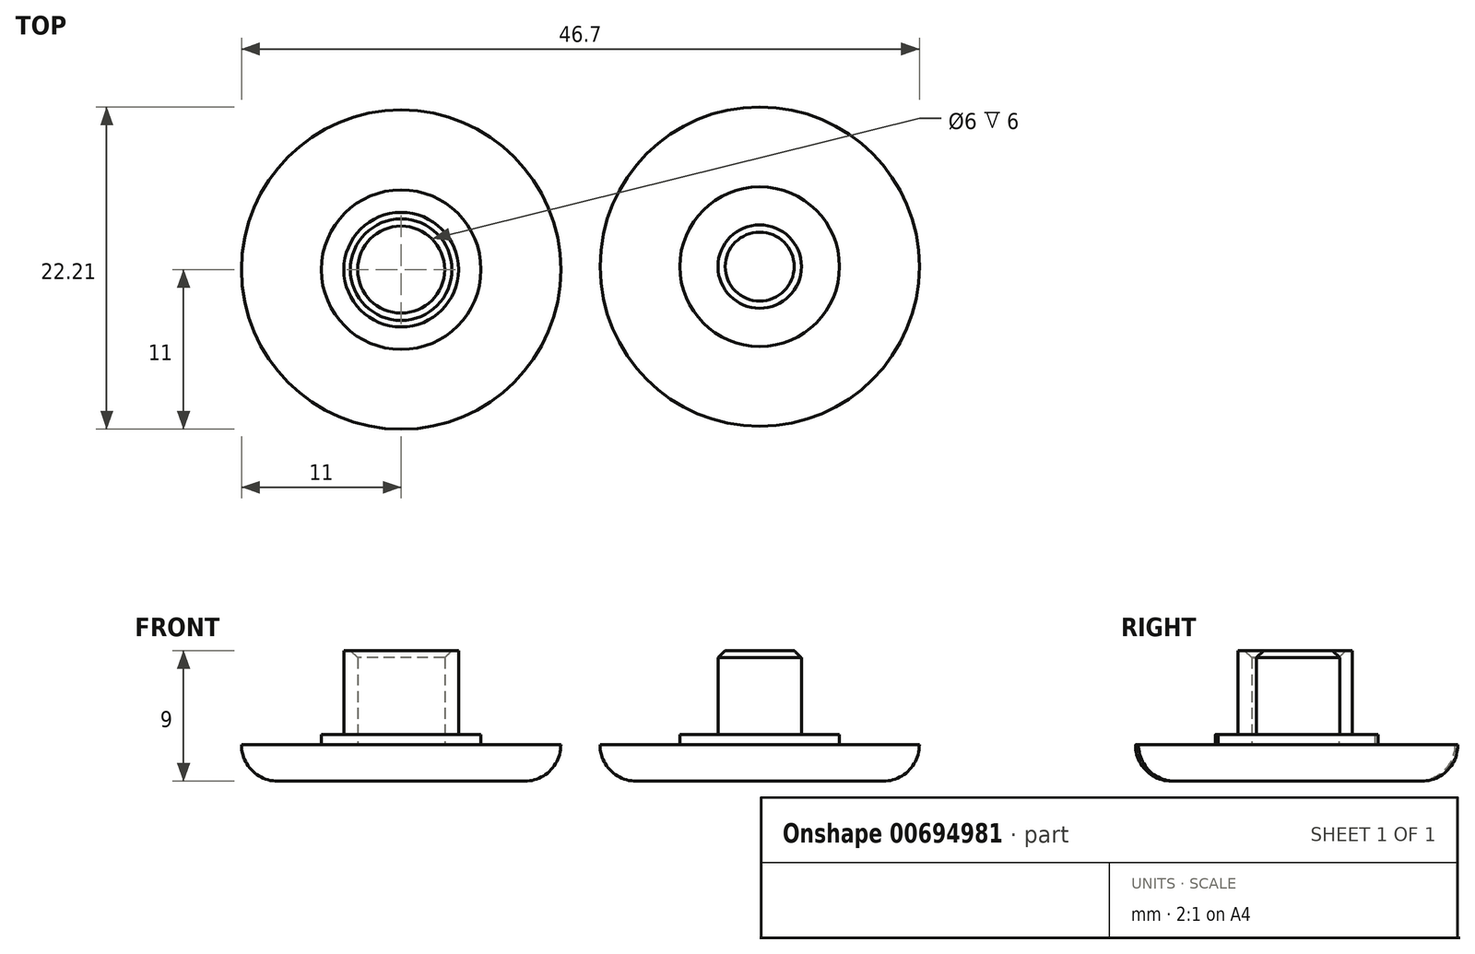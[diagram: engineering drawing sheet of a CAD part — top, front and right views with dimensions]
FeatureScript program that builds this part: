
annotation { "Feature Type Name" : "Feature", "Feature Type Description" : "" }
export const myFeature = defineFeature(function(context is Context, id is Id, definition is map)
    precondition{}
    {
        {
            var Q0;
            Q0=qCreatedBy(makeId("Top.planeOp"),FACE);
            var sketch = newSketch(context, id + "F0", { "sketchPlane" : qUnion([Q0])});
            skCircle(sketch, "E0", {"center": v(0, 0) * mm, "radius": 11 * mm});
            skCircle(sketch, "E1", {"center": v(0, 0) * mm, "radius": 5.5 * mm});
            skCircle(sketch, "E2", {"center": v(0, 0) * mm, "radius": 3.95 * mm});
            skCircle(sketch, "E3", {"center": v(24.7, 0.21) * mm, "radius": 11 * mm});
            skCircle(sketch, "E4", {"center": v(24.7, 0.21) * mm, "radius": 5.5 * mm});
            skCircle(sketch, "E5", {"center": v(24.7, 0.21) * mm, "radius": 3.95 * mm});
            skCircle(sketch, "E6", {"center": v(0, 0) * mm, "radius": 3 * mm});
            skCircle(sketch, "E7", {"center": v(24.7, 0.21) * mm, "radius": 2.88 * mm});
            skSolve(sketch);
        }
        {
            var Q0;
            Q0=makeQuery(id+"F0.imprint","IMPRINT",FACE,{"disambiguationData":[TD([[makeQuery(id+"F0.imprint","IMPRINT",EDGE,{"derivedFrom":sQuery(id+"F0.wireOp",EDGE,"E0")}),1.0]])]});
            extrude(context, id + "F1", {"entities" : qUnion([Q0]), "depth" : 2.5 * mm, "offsetDistance" : 25 * mm});
        }
        {
            var Q0;
            Q0=makeQuery(id+"F0.imprint","IMPRINT",FACE,{"disambiguationData":[TD([[makeQuery(id+"F0.imprint","IMPRINT",EDGE,{"derivedFrom":sQuery(id+"F0.wireOp",EDGE,"E1")}),1.0]])]});
            extrude(context, id + "F2", {"entities" : qUnion([Q0]), "operationType" : NewBodyOperationType.ADD, "depth" : 3.2 * mm, "offsetDistance" : 25 * mm});
        }
        {
            var Q0;
            Q0=makeQuery(id+"F0.imprint","IMPRINT",FACE,{"disambiguationData":[TD([[makeQuery(id+"F0.imprint","IMPRINT",EDGE,{"derivedFrom":sQuery(id+"F0.wireOp",EDGE,"E2")}),1.0]])]});
            extrude(context, id + "F3", {"entities" : qUnion([Q0]), "operationType" : NewBodyOperationType.ADD, "depth" : 9 * mm, "offsetDistance" : 25 * mm});
        }
        {
            var Q0;
            Q0=makeQuery(id+"F1.opExtrude","CAP_EDGE",EDGE,{"disambiguationData":[OSD([sQuery(id+"F0.wireOp",EDGE,"E0")])],"isStart":true});
            fillet(context, id + "F4", {"entities" : qUnion([Q0]), "radius" : 2.5 * mm, "tangentPropagation" : true, "allowEdgeOverflow" : false});
        }
        {
            var Q0;
            Q0=makeQuery(id+"F0.imprint","IMPRINT",FACE,{"disambiguationData":[TD([[makeQuery(id+"F0.imprint","IMPRINT",EDGE,{"derivedFrom":sQuery(id+"F0.wireOp",EDGE,"E6")}),1.0]])]});
            extrude(context, id + "F5", {"entities" : qUnion([Q0]), "operationType" : NewBodyOperationType.ADD, "depth" : 2.5 * mm, "offsetDistance" : 25 * mm});
        }
        {
            var Q0;
            Q0=makeQuery(id+"F0.imprint","IMPRINT",FACE,{"disambiguationData":[TD([[makeQuery(id+"F0.imprint","IMPRINT",EDGE,{"derivedFrom":sQuery(id+"F0.wireOp",EDGE,"E3")}),1.0]])]});
            extrude(context, id + "F6", {"entities" : qUnion([Q0]), "depth" : 2.5 * mm, "offsetDistance" : 25 * mm});
        }
        {
            var Q0;
            Q0=makeQuery(id+"F0.imprint","IMPRINT",FACE,{"disambiguationData":[TD([[makeQuery(id+"F0.imprint","IMPRINT",EDGE,{"derivedFrom":sQuery(id+"F0.wireOp",EDGE,"E4")}),1.0]])]});
            extrude(context, id + "F7", {"entities" : qUnion([Q0]), "operationType" : NewBodyOperationType.ADD, "depth" : 3.2 * mm, "offsetDistance" : 25 * mm});
        }
        {
            var Q0;
            Q0=makeQuery(id+"F0.imprint","IMPRINT",FACE,{"disambiguationData":[TD([[makeQuery(id+"F0.imprint","IMPRINT",EDGE,{"derivedFrom":sQuery(id+"F0.wireOp",EDGE,"E5")}),1.0]])]});
            extrude(context, id + "F8", {"entities" : qUnion([Q0]), "operationType" : NewBodyOperationType.ADD, "depth" : 3.2 * mm, "offsetDistance" : 25 * mm});
        }
        {
            var Q0;
            Q0=makeQuery(id+"F0.imprint","IMPRINT",FACE,{"disambiguationData":[TD([[makeQuery(id+"F0.imprint","IMPRINT",EDGE,{"derivedFrom":sQuery(id+"F0.wireOp",EDGE,"E7")}),1.0]])]});
            extrude(context, id + "F9", {"entities" : qUnion([Q0]), "operationType" : NewBodyOperationType.ADD, "depth" : 9 * mm, "offsetDistance" : 25 * mm});
        }
        {
            var Q0;
            Q0=makeQuery(id+"F6.opExtrude","CAP_EDGE",EDGE,{"disambiguationData":[OSD([sQuery(id+"F0.wireOp",EDGE,"E3")])],"isStart":true});
            fillet(context, id + "F10", {"entities" : qUnion([Q0]), "radius" : 2.5 * mm, "tangentPropagation" : true, "allowEdgeOverflow" : false});
        }
        {
            var Q0;
            Q0=makeQuery(id+"F9.opExtrude","CAP_EDGE",EDGE,{"disambiguationData":[OSD([sQuery(id+"F0.wireOp",EDGE,"E7")])],"isStart":false});
            chamfer(context, id + "F11", {"entities" : qUnion([Q0]), "width" : 0.5 * mm, "tangentPropagation" : true});
        }
        {
            var Q0;
            Q0=makeQuery(id+"F3.opExtrude","CAP_EDGE",EDGE,{"disambiguationData":[OSD([sQuery(id+"F0.wireOp",EDGE,"E6")])],"isStart":false});
            chamfer(context, id + "F12", {"entities" : qUnion([Q0]), "width" : 0.5 * mm, "tangentPropagation" : true});
        }
    });
